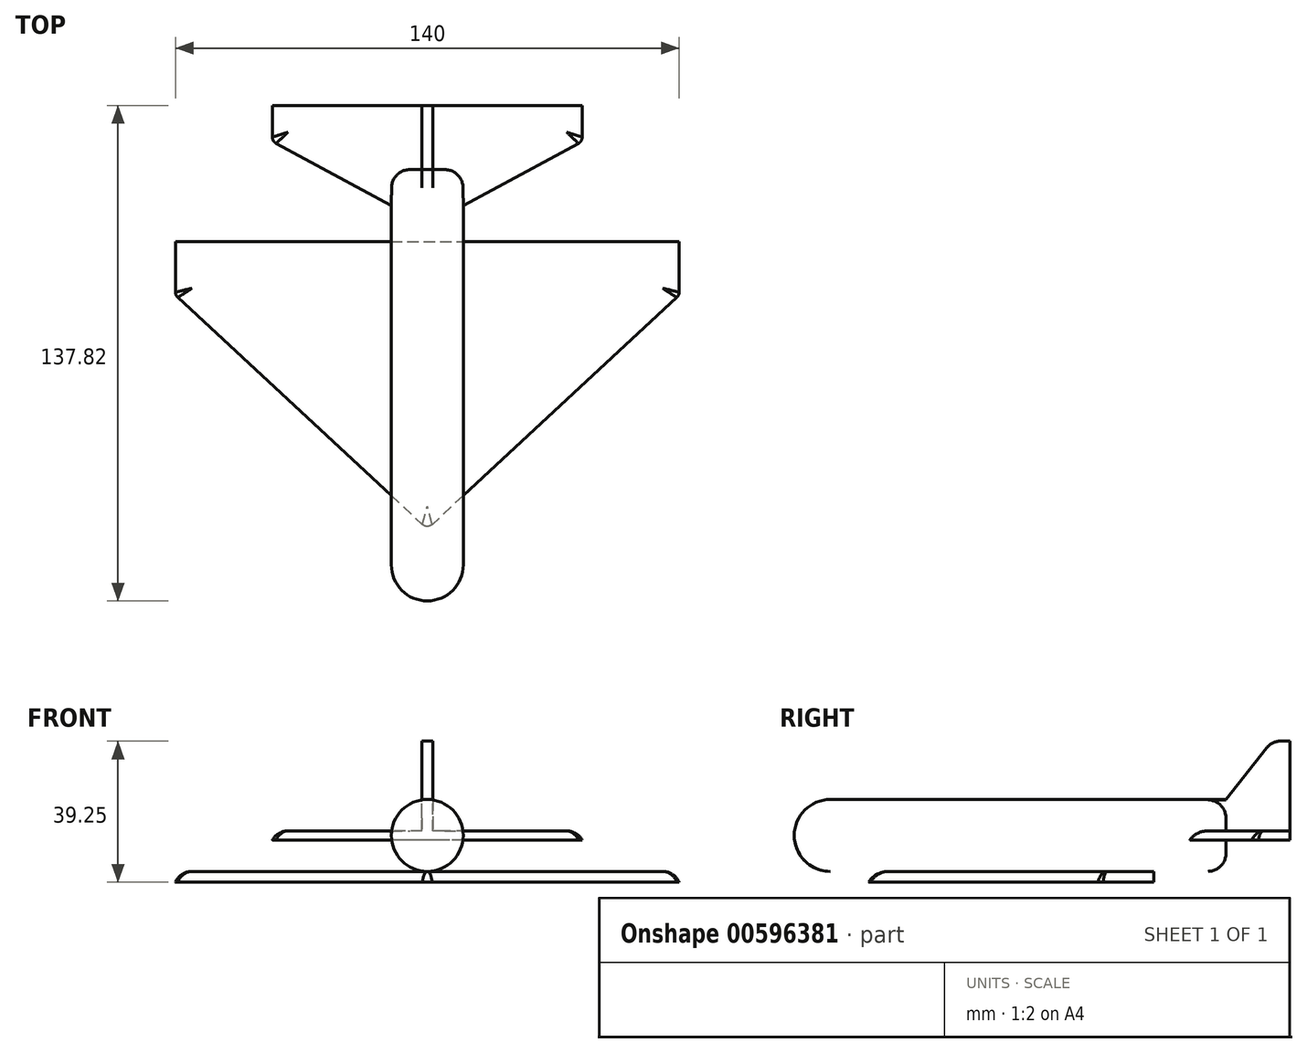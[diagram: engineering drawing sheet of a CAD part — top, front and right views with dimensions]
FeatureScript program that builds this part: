
annotation { "Feature Type Name" : "Feature", "Feature Type Description" : "" }
export const myFeature = defineFeature(function(context is Context, id is Id, definition is map)
    precondition{}
    {
        {
            var Q0;
            Q0=qCreatedBy(makeId("Top.planeOp"),FACE);
            var sketch = newSketch(context, id + "F0", { "sketchPlane" : qUnion([Q0])});
            skLineSegment(sketch, "E0", {"start": v(0, 0) * mm, "end": v(0, 40) * mm, "construction": true});
            skLineSegment(sketch, "E1", {"start": v(0, 0) * mm, "end": v(0, -40) * mm, "construction": true});
            skLineSegment(sketch, "E2", {"start": v(0, 40) * mm, "end": v(-70, 40) * mm});
            skLineSegment(sketch, "E3", {"start": v(-70, 40) * mm, "end": v(-70, 25) * mm});
            skLineSegment(sketch, "E4", {"start": v(-70, 25) * mm, "end": v(0, -40) * mm});
            skLineSegment(sketch, "E5.MirrorCS", {"start": v(0, 40) * mm, "end": v(70, 40) * mm});
            skLineSegment(sketch, "E6.MirrorCS", {"start": v(70, 40) * mm, "end": v(70, 25) * mm});
            skLineSegment(sketch, "E7", {"start": v(70, 25) * mm, "end": v(0, -40) * mm});
            skSolve(sketch);
        }
        {
            var Q0;
            Q0=qCreatedBy(makeId("Front.planeOp"),FACE);
            var sketch = newSketch(context, id + "F1", { "sketchPlane" : qUnion([Q0])});
            skCircle(sketch, "E8", {"center": v(0, 10) * mm, "radius": 10 * mm});
            skSolve(sketch);
        }
        {
            var Q0;
            Q0=makeQuery(id+"F0.imprint","IMPRINT",FACE,{"disambiguationData":[TD([[makeQuery(id+"F0.imprint","IMPRINT",EDGE,{"derivedFrom":sQuery(id+"F0.wireOp",EDGE,"E2")}),1.0]])]});
            extrude(context, id + "F2", {"entities" : qUnion([Q0]), "oppositeDirection" : true, "depth" : 3 * mm, "offsetDistance" : 25 * mm});
        }
        {
            var Q0;
            Q0=makeQuery(id+"F1.imprint","IMPRINT",FACE,{"disambiguationData":[TD([[makeQuery(id+"F1.imprint","IMPRINT",EDGE,{"derivedFrom":sQuery(id+"F1.wireOp",EDGE,"E8")}),1.0]])]});
            extrude(context, id + "F3", {"entities" : qUnion([Q0]), "endBound" : BoundingType.SYMMETRIC, "depth" : 120 * mm, "offsetDistance" : 25 * mm});
        }
        {
            var Q0;
            Q0=qCreatedBy(makeId("Top.planeOp"),FACE);
            cPlane(context, id + "F4", {"entities" : qUnion([Q0]), "cplaneType" : CPlaneType.OFFSET, "offset" : 10 * mm, "width" : 150 * mm, "height" : 150 * mm});
        }
        {
            var Q0;
            Q0=qCreatedBy(id+"F4.planeOp",FACE);
            var sketch = newSketch(context, id + "F5", { "sketchPlane" : qUnion([Q0])});
            skLineSegment(sketch, "E9", {"start": v(10, 60) * mm, "end": v(10, -30.7) * mm});
            skLineSegment(sketch, "E10", {"start": v(-10, -30.7) * mm, "end": v(-10, 60) * mm});
            skLineSegment(sketch, "E11.0.0", {"start": v(0, -40) * mm, "end": v(70, 25) * mm});
            skLineSegment(sketch, "E11.0.1", {"start": v(70, 25) * mm, "end": v(70, 40) * mm});
            skLineSegment(sketch, "E11.0.2", {"start": v(70, 40) * mm, "end": v(0, 40) * mm});
            skLineSegment(sketch, "E11.0.3", {"start": v(0, 40) * mm, "end": v(-70, 40) * mm});
            skLineSegment(sketch, "E11.0.4", {"start": v(-70, 40) * mm, "end": v(-70, 25) * mm});
            skLineSegment(sketch, "E11.0.5", {"start": v(-70, 25) * mm, "end": v(0, -40) * mm});
            skLineSegment(sketch, "E12", {"start": v(-10, 60) * mm, "end": v(-10, 50) * mm, "construction": true});
            skLineSegment(sketch, "E13", {"start": v(-10, 50) * mm, "end": v(-43.05, 67.82) * mm});
            skLineSegment(sketch, "E14", {"start": v(-43.05, 67.82) * mm, "end": v(-43.05, 77.82) * mm});
            skLineSegment(sketch, "E15", {"start": v(-43.05, 77.82) * mm, "end": v(0, 77.82) * mm});
            skLineSegment(sketch, "E16", {"start": v(0, 77.82) * mm, "end": v(0, 0) * mm, "construction": true});
            skLineSegment(sketch, "E17.MirrorCS", {"start": v(43.05, 67.82) * mm, "end": v(43.05, 77.82) * mm});
            skLineSegment(sketch, "E18.MirrorCS", {"start": v(43.05, 77.82) * mm, "end": v(0, 77.82) * mm});
            skLineSegment(sketch, "E19.MirrorCS", {"start": v(10, 50) * mm, "end": v(43.05, 67.82) * mm});
            skLineSegment(sketch, "E20", {"start": v(-10, 50) * mm, "end": v(10, 50) * mm});
            skLineSegment(sketch, "E21.0", {"start": v(10, -60) * mm, "end": v(-10, -60) * mm});
            skSolve(sketch);
        }
        {
            var Q0;
            Q0=makeQuery(id+"F5.imprint","IMPRINT",FACE,{"disambiguationData":[TD([[makeQuery(id+"F5.imprint","IMPRINT",EDGE,{"derivedFrom":sQuery(id+"F5.wireOp",EDGE,"E13")}),-1.0]])]});
            extrude(context, id + "F6", {"entities" : qUnion([Q0]), "operationType" : NewBodyOperationType.ADD, "endBound" : BoundingType.SYMMETRIC, "depth" : 2.5 * mm, "offsetDistance" : 25 * mm});
        }
        {
            var Q0;
            Q0=qCreatedBy(makeId("Right.planeOp"),FACE);
            var sketch = newSketch(context, id + "F7", { "sketchPlane" : qUnion([Q0])});
            skLineSegment(sketch, "E22.0.0", {"start": v(77.82, 8.75) * mm, "end": v(67.82, 8.75) * mm});
            skLineSegment(sketch, "E22.0.1", {"start": v(67.82, 8.75) * mm, "end": v(67.82, 11.25) * mm});
            skLineSegment(sketch, "E22.0.2", {"start": v(67.82, 11.25) * mm, "end": v(77.82, 11.25) * mm});
            skLineSegment(sketch, "E22.0.3", {"start": v(77.82, 11.25) * mm, "end": v(77.82, 8.75) * mm});
            skLineSegment(sketch, "E23.0.0", {"start": v(67.82, 8.75) * mm, "end": v(50, 8.75) * mm});
            skLineSegment(sketch, "E23.0.1", {"start": v(50, 8.75) * mm, "end": v(50, 10) * mm});
            skLineSegment(sketch, "E23.0.2", {"start": v(50, 10) * mm, "end": v(50, 11.25) * mm});
            skLineSegment(sketch, "E23.0.3", {"start": v(50, 11.25) * mm, "end": v(67.82, 11.25) * mm});
            skLineSegment(sketch, "E23.0.4", {"start": v(67.82, 11.25) * mm, "end": v(67.82, 8.75) * mm});
            skLineSegment(sketch, "E24", {"start": v(77.82, 11.25) * mm, "end": v(77.82, 36.25) * mm});
            skLineSegment(sketch, "E25", {"start": v(77.82, 36.25) * mm, "end": v(72.82, 36.25) * mm});
            skLineSegment(sketch, "E26", {"start": v(60, 0) * mm, "end": v(-60, 0) * mm});
            skLineSegment(sketch, "E27", {"start": v(-60, 20) * mm, "end": v(60, 20) * mm});
            skLineSegment(sketch, "E28", {"start": v(72.82, 36.25) * mm, "end": v(60, 20) * mm});
            skLineSegment(sketch, "E29", {"start": v(60, 20) * mm, "end": v(60, 11.25) * mm});
            skPoint(sketch, "E29.endSnap0", {"position": v(58.9, 11.25) * mm});
            skSolve(sketch);
        }
        {
            var Q0;
            {var subQ1=sQuery(id+"F7.wireOp",EDGE,"E22.0.2");Q0=makeQuery(id+"F7.imprint","IMPRINT",FACE,{"disambiguationData":[TD([[makeQuery(id+"F7.imprint","IMPRINT",EDGE,{"derivedFrom":subQ1}),1.0]])]});}
            extrude(context, id + "F8", {"entities" : qUnion([Q0]), "operationType" : NewBodyOperationType.ADD, "endBound" : BoundingType.SYMMETRIC, "depth" : 3 * mm, "offsetDistance" : 25 * mm});
        }
        {
            var Q0;
            Q0=makeQuery(id+"F2.opExtrude","SWEPT_EDGE",EDGE,{"disambiguationData":[OSD([sQuery(id+"F0.wireOp",EDGE,"E4"),sQuery(id+"F0.wireOp",EDGE,"E7")])]});
            var Q1;
            Q1=makeQuery(id+"F2.opExtrude","SWEPT_EDGE",EDGE,{"disambiguationData":[OSD([sQuery(id+"F0.wireOp",EDGE,"E6.MirrorCS"),sQuery(id+"F0.wireOp",EDGE,"E7")])]});
            var Q2;
            Q2=makeQuery(id+"F2.opExtrude","SWEPT_EDGE",EDGE,{"disambiguationData":[OSD([sQuery(id+"F0.wireOp",EDGE,"E3"),sQuery(id+"F0.wireOp",EDGE,"E4")])]});
            var Q3;
            Q3=makeQuery(id+"F6.opExtrude","SWEPT_EDGE",EDGE,{"disambiguationData":[OSD([sQuery(id+"F5.wireOp",EDGE,"E17.MirrorCS"),sQuery(id+"F5.wireOp",EDGE,"E19.MirrorCS")])]});
            var Q4;
            Q4=makeQuery(id+"F6.opExtrude","SWEPT_EDGE",EDGE,{"disambiguationData":[OSD([sQuery(id+"F5.wireOp",EDGE,"E13"),sQuery(id+"F5.wireOp",EDGE,"E14")])]});
            fillet(context, id + "F9", {"entities" : qUnion([Q0, Q1, Q2, Q3, Q4]), "radius" : 2 * mm, "tangentPropagation" : true, "allowEdgeOverflow" : false});
        }
        {
            var Q0;
            {var subQ0=sQuery(id+"F7.wireOp",EDGE,"E29");var subQ1=sQuery(id+"F1.wireOp",EDGE,"E8");var subQ2=makeQuery(id+"F3.opExtrude","SWEPT_FACE",FACE,{"disambiguationData":[OSD([subQ1])]});var subQ3=makeQuery(id+"F6.opExtrude","CAP_FACE",FACE,{"disambiguationData":[OSD([sQuery(id+"F5.wireOp",EDGE,"E13"),sQuery(id+"F5.wireOp",EDGE,"E14"),sQuery(id+"F5.wireOp",EDGE,"E15"),sQuery(id+"F5.wireOp",EDGE,"E17.MirrorCS"),sQuery(id+"F5.wireOp",EDGE,"E18.MirrorCS"),sQuery(id+"F5.wireOp",EDGE,"E19.MirrorCS"),sQuery(id+"F5.wireOp",EDGE,"E20")])],"isStart":false});var subQ4=makeQuery(id+"F3.opExtrude","CAP_FACE",FACE,{"disambiguationData":[OSD([subQ1])],"isStart":true});Q0=makeQuery(id+"F8.boolean.opBoolean","SPLIT",EDGE,{"disambiguationData":[topologyDisambiguationEdgeConnected([subQ2,subQ4]),TD([makeQuery(id+"F8.opExtrude","CAP_FACE",FACE,{"disambiguationData":[OSD([sQuery(id+"F7.wireOp",EDGE,"E22.0.2"),sQuery(id+"F7.wireOp",EDGE,"E24"),sQuery(id+"F7.wireOp",EDGE,"E25"),sQuery(id+"F7.wireOp",EDGE,"E23.0.3"),sQuery(id+"F7.wireOp",EDGE,"E28"),subQ0])],"isStart":false})])],"derivedFrom":makeQuery(id+"F6.boolean.opBoolean","SPLIT",EDGE,{"disambiguationData":[TD([subQ3])],"derivedFrom":makeQuery(id+"F3.opExtrude","CAP_EDGE",EDGE,{"disambiguationData":[OSD([subQ1])],"isStart":true})})});}
            var Q1;
            {var subQ0=sQuery(id+"F1.wireOp",EDGE,"E8");Q1=makeQuery(id+"F6.boolean.opBoolean","SPLIT",EDGE,{"disambiguationData":[TD([makeQuery(id+"F6.opExtrude","CAP_FACE",FACE,{"disambiguationData":[OSD([sQuery(id+"F5.wireOp",EDGE,"E13"),sQuery(id+"F5.wireOp",EDGE,"E14"),sQuery(id+"F5.wireOp",EDGE,"E15"),sQuery(id+"F5.wireOp",EDGE,"E17.MirrorCS"),sQuery(id+"F5.wireOp",EDGE,"E18.MirrorCS"),sQuery(id+"F5.wireOp",EDGE,"E19.MirrorCS"),sQuery(id+"F5.wireOp",EDGE,"E20")])],"isStart":true})])],"derivedFrom":makeQuery(id+"F3.opExtrude","CAP_EDGE",EDGE,{"disambiguationData":[OSD([subQ0])],"isStart":true})});}
            var Q2;
            {var subQ0=sQuery(id+"F7.wireOp",EDGE,"E29");var subQ1=makeQuery(id+"F6.opExtrude","CAP_FACE",FACE,{"disambiguationData":[OSD([sQuery(id+"F5.wireOp",EDGE,"E13"),sQuery(id+"F5.wireOp",EDGE,"E14"),sQuery(id+"F5.wireOp",EDGE,"E15"),sQuery(id+"F5.wireOp",EDGE,"E17.MirrorCS"),sQuery(id+"F5.wireOp",EDGE,"E18.MirrorCS"),sQuery(id+"F5.wireOp",EDGE,"E19.MirrorCS"),sQuery(id+"F5.wireOp",EDGE,"E20")])],"isStart":false});var subQ2=sQuery(id+"F1.wireOp",EDGE,"E8");var subQ3=makeQuery(id+"F3.opExtrude","CAP_FACE",FACE,{"disambiguationData":[OSD([subQ2])],"isStart":true});var subQ4=makeQuery(id+"F3.opExtrude","SWEPT_FACE",FACE,{"disambiguationData":[OSD([subQ2])]});Q2=makeQuery(id+"F8.boolean.opBoolean","SPLIT",EDGE,{"disambiguationData":[topologyDisambiguationEdgeConnected([subQ4,subQ3]),TD([makeQuery(id+"F8.opExtrude","CAP_FACE",FACE,{"disambiguationData":[OSD([sQuery(id+"F7.wireOp",EDGE,"E22.0.2"),sQuery(id+"F7.wireOp",EDGE,"E24"),sQuery(id+"F7.wireOp",EDGE,"E25"),sQuery(id+"F7.wireOp",EDGE,"E23.0.3"),sQuery(id+"F7.wireOp",EDGE,"E28"),subQ0])],"isStart":true})])],"derivedFrom":makeQuery(id+"F6.boolean.opBoolean","SPLIT",EDGE,{"disambiguationData":[TD([subQ1])],"derivedFrom":makeQuery(id+"F3.opExtrude","CAP_EDGE",EDGE,{"disambiguationData":[OSD([subQ2])],"isStart":true})})});}
            fillet(context, id + "F10", {"entities" : qUnion([Q0, Q1, Q2]), "radius" : 5 * mm, "tangentPropagation" : true, "allowEdgeOverflow" : false});
        }
        {
            var Q0;
            Q0=makeQuery(id+"F3.opExtrude","CAP_FACE",FACE,{"disambiguationData":[OSD([sQuery(id+"F1.wireOp",EDGE,"E8")])],"isStart":false});
            fillet(context, id + "F11", {"entities" : qUnion([Q0]), "radius" : 10 * mm, "allowEdgeOverflow" : false});
        }
        {
            var Q0;
            Q0=makeQuery(id+"F2.opExtrude","CAP_EDGE",EDGE,{"disambiguationData":[OSD([sQuery(id+"F0.wireOp",EDGE,"E7")])],"isStart":true});
            var Q1;
            Q1=makeQuery(id+"F6.opExtrude","CAP_EDGE",EDGE,{"disambiguationData":[OSD([sQuery(id+"F5.wireOp",EDGE,"E19.MirrorCS")])],"isStart":false});
            var Q2;
            Q2=makeQuery(id+"F6.opExtrude","CAP_EDGE",EDGE,{"disambiguationData":[OSD([sQuery(id+"F5.wireOp",EDGE,"E13")])],"isStart":false});
            fillet(context, id + "F12", {"entities" : qUnion([Q0, Q1, Q2]), "radius" : 5 * mm, "tangentPropagation" : true, "allowEdgeOverflow" : false});
        }
        {
            var Q0;
            Q0=makeQuery(id+"F8.opExtrude","SWEPT_EDGE",EDGE,{"disambiguationData":[OSD([sQuery(id+"F7.wireOp",EDGE,"E25"),sQuery(id+"F7.wireOp",EDGE,"E28")])]});
            fillet(context, id + "F13", {"entities" : qUnion([Q0]), "radius" : 5 * mm, "tangentPropagation" : true, "allowEdgeOverflow" : false});
        }
    });
